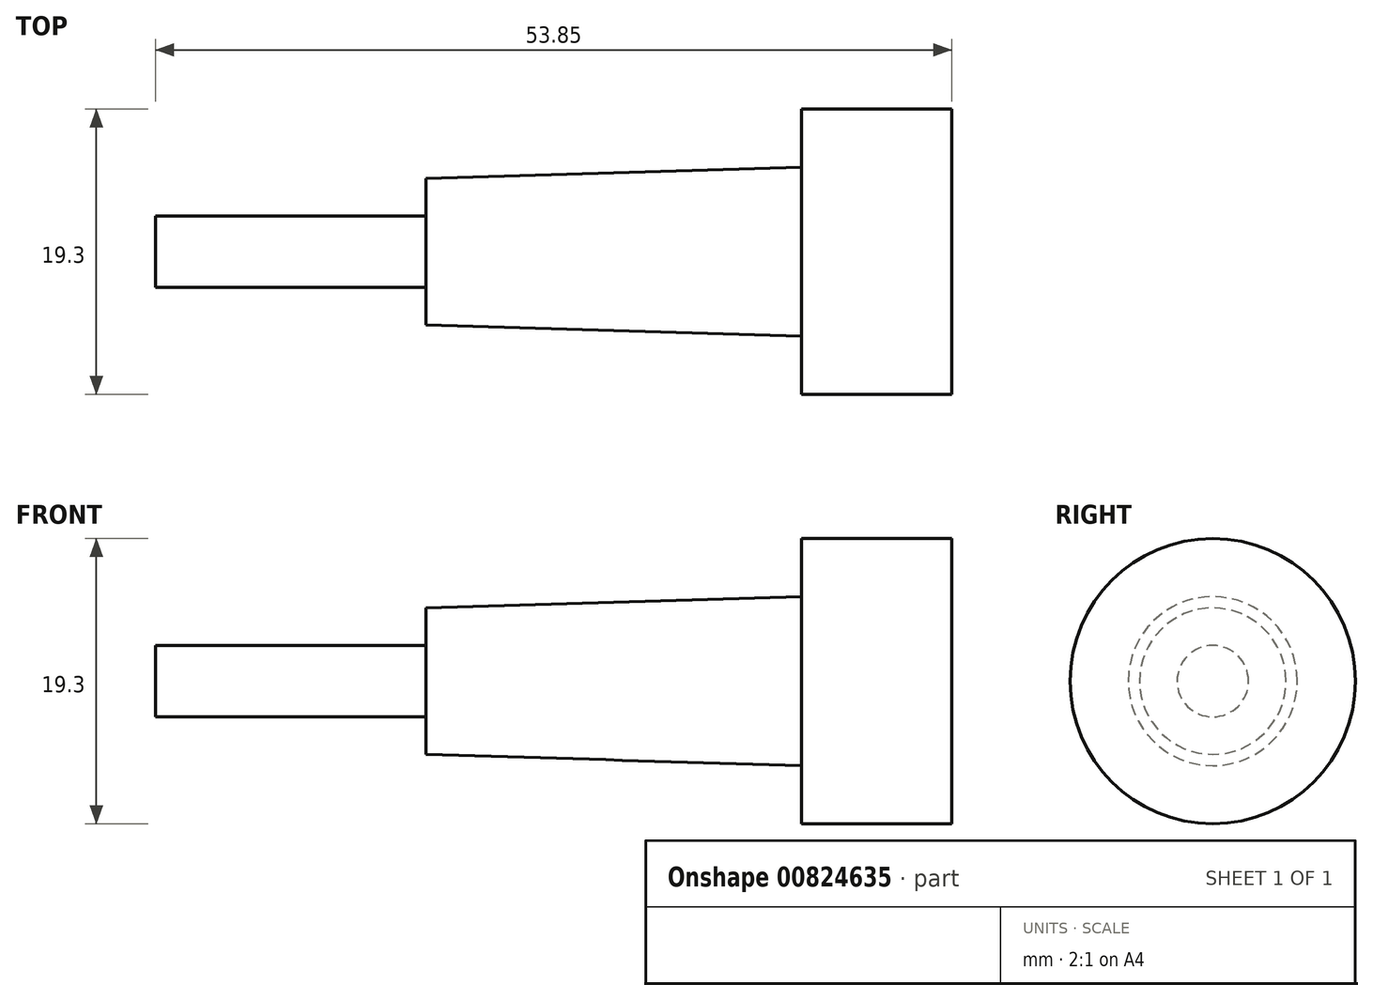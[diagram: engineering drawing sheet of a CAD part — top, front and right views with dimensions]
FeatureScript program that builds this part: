
annotation { "Feature Type Name" : "Feature", "Feature Type Description" : "" }
export const myFeature = defineFeature(function(context is Context, id is Id, definition is map)
    precondition{}
    {
        {
            var Q0;
            Q0=qCreatedBy(makeId("Right.planeOp"),FACE);
            var sketch = newSketch(context, id + "F0", { "sketchPlane" : qUnion([Q0])});
            skCircle(sketch, "E0", {"center": v(0, 0) * mm, "radius": 4.95 * mm});
            skSolve(sketch);
        }
        {
            var Q0;
            Q0=qCreatedBy(makeId("Right.planeOp"),FACE);
            cPlane(context, id + "F1", {"entities" : qUnion([Q0]), "cplaneType" : CPlaneType.OFFSET, "offset" : 25.4 * mm, "width" : 152.4 * mm, "height" : 152.4 * mm});
        }
        {
            var Q0;
            Q0=qCreatedBy(id+"F1.planeOp",FACE);
            var sketch = newSketch(context, id + "F2", { "sketchPlane" : qUnion([Q0])});
            skCircle(sketch, "E1", {"center": v(0, 0) * mm, "radius": 5.72 * mm});
            skSolve(sketch);
        }
        {
            var Q0;
            Q0=makeQuery(id+"F0.imprint","IMPRINT",FACE,{"disambiguationData":[TD([[makeQuery(id+"F0.imprint","IMPRINT",EDGE,{"derivedFrom":sQuery(id+"F0.wireOp",EDGE,"E0")}),1.0]])]});
            var Q1;
            Q1=makeQuery(id+"F2.imprint","IMPRINT",FACE,{"disambiguationData":[TD([[makeQuery(id+"F2.imprint","IMPRINT",EDGE,{"derivedFrom":sQuery(id+"F2.wireOp",EDGE,"E1")}),1.0]])]});
            loft(context, id + "F3", {"sheetProfilesArray" : [{ "sheetProfileEntities" : qUnion([Q0]) }, { "sheetProfileEntities" : qUnion([Q1]) }]});
        }
        {
            var Q0;
            Q0=makeQuery(id+"F3.opLoft","CAP_FACE",FACE,{"disambiguationData":[OSD([makeQuery(id+"F0.imprint","IMPRINT",FACE,{"disambiguationData":[TD([[makeQuery(id+"F0.imprint","IMPRINT",EDGE,{"derivedFrom":sQuery(id+"F0.wireOp",EDGE,"E0")}),1.0]])]})])],"isStart":true});
            var sketch = newSketch(context, id + "F4", { "sketchPlane" : qUnion([Q0])});
            skCircle(sketch, "E2", {"center": v(0, 0) * mm, "radius": 2.41 * mm});
            skSolve(sketch);
        }
        {
            var Q0;
            Q0=makeQuery(id+"F4.imprint","IMPRINT",FACE,{"disambiguationData":[TD([[makeQuery(id+"F4.imprint","IMPRINT",EDGE,{"derivedFrom":sQuery(id+"F4.wireOp",EDGE,"E2")}),1.0]])]});
            extrude(context, id + "F5", {"entities" : qUnion([Q0]), "operationType" : NewBodyOperationType.ADD, "depth" : 18.29 * mm, "offsetDistance" : 25.4 * mm});
        }
        {
            var Q0;
            Q0=makeQuery(id+"F3.opLoft","CAP_FACE",FACE,{"disambiguationData":[OSD([makeQuery(id+"F2.imprint","IMPRINT",FACE,{"disambiguationData":[TD([[makeQuery(id+"F2.imprint","IMPRINT",EDGE,{"derivedFrom":sQuery(id+"F2.wireOp",EDGE,"E1")}),1.0]])]})])],"isStart":true});
            var sketch = newSketch(context, id + "F6", { "sketchPlane" : qUnion([Q0])});
            skCircle(sketch, "E3", {"center": v(0, 0) * mm, "radius": 9.65 * mm});
            skSolve(sketch);
        }
        {
            var Q0;
            Q0=makeQuery(id+"F6.imprint","IMPRINT",FACE,{"disambiguationData":[TD([[makeQuery(id+"F6.imprint","IMPRINT",EDGE,{"derivedFrom":sQuery(id+"F6.wireOp",EDGE,"E3")}),1.0]])]});
            var Q1;
            Q1=makeQuery(id+"F6.imprint","IMPRINT",FACE,{"disambiguationData":[TD([[makeQuery(id+"F6.imprint","IMPRINT",EDGE,{"derivedFrom":makeQuery(id+"F3.opLoft","MID_CAP_EDGE",EDGE,{"disambiguationData":[OSD([sQuery(id+"F2.wireOp",EDGE,"E1")])],"capPos":1.0})}),1.0]])]});
            var Q2;
            Q2=sQuery(id+"F6.wireOp",EDGE,"E3");
            extrude(context, id + "F7", {"entities" : qUnion([Q0, Q1]), "operationType" : NewBodyOperationType.ADD, "surfaceEntities" : qUnion([Q2]), "depth" : 10.16 * mm, "offsetDistance" : 25.4 * mm});
        }
    });
